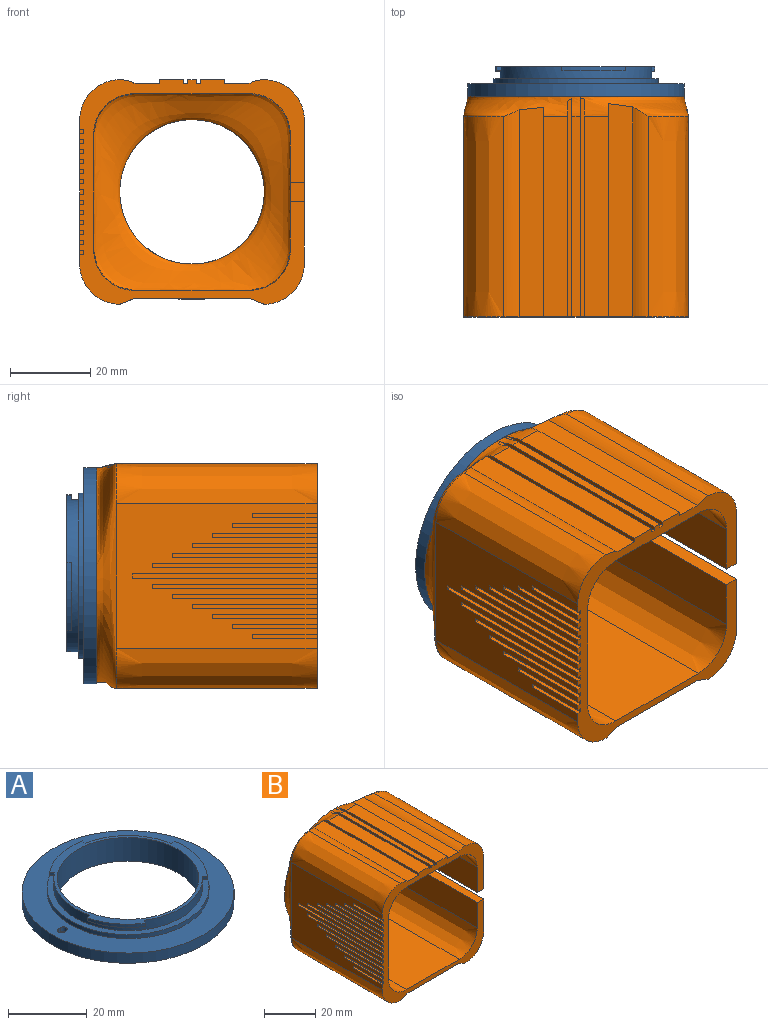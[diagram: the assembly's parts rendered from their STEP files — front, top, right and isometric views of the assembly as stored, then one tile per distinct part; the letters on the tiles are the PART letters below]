
ASSEMBLY  parts=2 mates=1
PART A: 25 faces, bbox 54x54x7.4 mm
  f0: cylinder r=18.92mm len=37.85mm, axis (0,0,-1), area 300.8mm2, adj f6,f7,f8,f10,f11,f13,f14,f15
  f1: cylinder r=18.03mm len=36.07mm, axis (0,0,-1), area 836.1mm2, adj f4,f7
  f2: cylinder r=27mm len=54mm, axis (0,0,-1), area 538.6mm2, adj f3,f4
  f3: plane 54x54mm, normal (0,0,1), area 948.2mm2, adj f2,f5,f20,f21,f22,f23
  f4: plane 54x54mm, normal (0,0,-1), area 1268.5mm2, adj f1,f2
  f5: cylinder r=20.63mm len=41.26mm, axis (0,0,-1), area 164.6mm2, adj f3,f6
  f6: plane 41.26x41.26mm, normal (0,0,1), area 212.3mm2, adj f0,f5
  f7: plane 39.82x39.14mm, normal (0,0,1), area 166.2mm2, adj f0,f1,f8,f9,f10,f12,f13,f14
  f8: plane 1.27x1.02mm, normal (0.98,-0.17,0), area 1.3mm2, adj f0,f7,f9,f11
  f9: cylinder r=20.21mm len=15.81mm, axis (0,0,1), area 17mm2, adj f7,f8,f10,f11
  f10: plane 1.02x1.02mm, normal (-0.79,-0.61,0), area 1.3mm2, adj f0,f7,f9,f11
  f11: plane 15.81x5.2mm, normal (0,0,-1), area 20.9mm2, adj f0,f8,f9,f10
  f12: cylinder r=20.21mm len=12.16mm, axis (0,0,1), area 15.6mm2, adj f7,f13,f14,f15
  f13: plane 1.09x1.02mm, normal (0.84,-0.54,0), area 1.3mm2, adj f0,f7,f12,f15
  f14: plane 1.25x1.02mm, normal (-0.24,0.97,0), area 1.3mm2, adj f0,f7,f12,f15
  f15: plane 12.47x9.44mm, normal (0,0,-1), area 19.2mm2, adj f0,f12,f13,f14
  f16: plane 1.27x1.02mm, normal (-0.17,0.99,0), area 1.3mm2, adj f0,f7,f18,f19
  f17: plane 1.02x0.95mm, normal (-0.68,-0.74,0), area 1.3mm2, adj f0,f7,f18,f19
  f18: cylinder r=20.21mm len=16.99mm, axis (0,0,1), area 18.6mm2, adj f7,f16,f17,f19
  f19: plane 16.99x6.26mm, normal (0,0,-1), area 22.9mm2, adj f0,f16,f17,f18
  f20: cylinder r=1.02mm len=2.03mm, axis (0,0,1), area 4.1mm2, adj f3,f21,f23,f24
  f21: plane 1.27x0.76mm, normal (0,-1,0), area 1mm2, adj f3,f20,f22,f24
  f22: cylinder r=1.02mm len=2.03mm, axis (0,0,1), area 4.1mm2, adj f3,f21,f23,f24
  f23: plane 1.27x0.76mm, normal (0,1,0), area 1mm2, adj f3,f20,f22,f24
  f24: plane 2.79x2.03mm, normal (0,0,1), area 4.8mm2, adj f20,f21,f22,f23
PART B: 120 faces, bbox 56.8x55.8x56.8 mm
  f0: plane 50x15.6mm, normal (1,0,0), area 460mm2, adj f2,f6,f10,f11,f99,f100,f101,f102
  f1: plane 54.46x53.95mm, normal (0,1,0), area 1265.1mm2, adj f2,f9,f92
  f2: bspline ~56x56mm, area 1121.8mm2, adj f0,f1,f3,f4,f5,f7,f8,f11
  f3: plane 50.07x6.07mm, normal (0,0,1), area 300mm2, adj f2,f6,f84,f89
  f4: plane 50x2mm, normal (0,0,1), area 100mm2, adj f2,f6,f78,f86
  f5: plane 50.07x6.07mm, normal (0,0,1), area 300mm2, adj f2,f6,f80,f81
  f6: plane 56x56mm, normal (0,-1,0), area 640mm2, adj f0,f3,f4,f5,f7,f10,f11,f12
  f7: plane 50x36mm, normal (-1,0,0), area 1412mm2, adj f2,f6,f12,f13,f26,f27,f28,f30
  f8: plane 4.8x3.5mm, normal (0,-1,0), area 16.8mm2, adj f2,f9,f10,f16
  f9: bspline ~49x49mm, area 1542.6mm2, adj f1,f8,f17,f18,f19,f20,f21,f22
  f10: plane 50x3.5mm, normal (0,0,-1), area 175mm2, adj f0,f6,f8,f25
  f11: extruded ~50x10mm, area 785.4mm2, adj f0,f2,f6,f83
  f12: extruded ~50x10mm, area 785.4mm2, adj f2,f6,f7,f87
  f13: extruded ~50x10mm, area 785.4mm2, adj f2,f6,f7,f90
  f14: extruded ~50x10mm, area 785.4mm2, adj f2,f6,f15,f91
  f15: plane 50x15.6mm, normal (1,0,0), area 544.4mm2, adj f2,f6,f14,f16,f93,f95,f97
  f16: plane 50x3.5mm, normal (0,0,1), area 175mm2, adj f6,f8,f15,f17
  f17: plane 50.66x12.76mm, normal (-1,0,0), area 605mm2, adj f6,f9,f16,f18
  f18: extruded ~50x10mm, area 785.4mm2, adj f6,f9,f17,f19
  f19: plane 50.81x29.81mm, normal (0,0,1), area 1450mm2, adj f6,f9,f18,f20
  f20: extruded ~50x10mm, area 785.4mm2, adj f6,f9,f19,f21
  f21: plane 50.81x29.81mm, normal (1,0,0), area 1450mm2, adj f6,f9,f20,f22
  f22: extruded ~50x10mm, area 785.4mm2, adj f6,f9,f21,f23
  f23: plane 50.81x29.81mm, normal (0,0,-1), area 1450mm2, adj f6,f9,f22,f24
  f24: extruded ~50x10mm, area 785.4mm2, adj f6,f9,f23,f25
  f25: plane 50.66x12.76mm, normal (-1,0,0), area 605mm2, adj f6,f9,f10,f24
  f26: plane 46x1mm, normal (0,0,-1), area 46mm2, adj f6,f7,f27,f29
  f27: plane 1x1mm, normal (0,-1,0), area 1mm2, adj f7,f26,f28,f29
  f28: plane 46x1mm, normal (0,0,1), area 46mm2, adj f6,f7,f27,f29
  f29: plane 46x1mm, normal (-1,0,0), area 46mm2, adj f6,f26,f27,f28
  f30: plane 1x1mm, normal (0,-1,0), area 1mm2, adj f7,f31,f32,f33
  f31: plane 21x1mm, normal (0,0,1), area 21mm2, adj f6,f7,f30,f33
  f32: plane 21x1mm, normal (0,0,-1), area 21mm2, adj f6,f7,f30,f33
  f33: plane 21x1mm, normal (-1,0,0), area 21mm2, adj f6,f30,f31,f32
  f34: plane 1x1mm, normal (0,-1,0), area 1mm2, adj f7,f35,f36,f37
  f35: plane 31x1mm, normal (0,0,1), area 31mm2, adj f6,f7,f34,f37
  f36: plane 31x1mm, normal (0,0,-1), area 31mm2, adj f6,f7,f34,f37
  f37: plane 31x1mm, normal (-1,0,0), area 31mm2, adj f6,f34,f35,f36
  f38: plane 16x1mm, normal (0,0,1), area 16mm2, adj f6,f7,f40,f41
  f39: plane 16x1mm, normal (0,0,-1), area 16mm2, adj f6,f7,f40,f41
  f40: plane 1x1mm, normal (0,-1,0), area 1mm2, adj f7,f38,f39,f41
  f41: plane 16x1mm, normal (-1,0,0), area 16mm2, adj f6,f38,f39,f40
  f42: plane 16x1mm, normal (0,0,-1), area 16mm2, adj f6,f7,f43,f45
  f43: plane 1x1mm, normal (0,-1,0), area 1mm2, adj f7,f42,f44,f45
  f44: plane 16x1mm, normal (0,0,1), area 16mm2, adj f6,f7,f43,f45
  f45: plane 16x1mm, normal (-1,0,0), area 16mm2, adj f6,f42,f43,f44
  f46: plane 41x1mm, normal (0,0,1), area 41mm2, adj f6,f7,f48,f49
  f47: plane 41x1mm, normal (0,0,-1), area 41mm2, adj f6,f7,f48,f49
  f48: plane 1x1mm, normal (0,-1,0), area 1mm2, adj f7,f46,f47,f49
  f49: plane 41x1mm, normal (-1,0,0), area 41mm2, adj f6,f46,f47,f48
  f50: plane 36x1mm, normal (0,0,1), area 36mm2, adj f6,f7,f52,f53
  f51: plane 36x1mm, normal (0,0,-1), area 36mm2, adj f6,f7,f52,f53
  f52: plane 1x1mm, normal (0,-1,0), area 1mm2, adj f7,f50,f51,f53
  f53: plane 36x1mm, normal (-1,0,0), area 36mm2, adj f6,f50,f51,f52
  f54: plane 31x1mm, normal (0,0,1), area 31mm2, adj f6,f7,f56,f57
  f55: plane 31x1mm, normal (0,0,-1), area 31mm2, adj f6,f7,f56,f57
  f56: plane 1x1mm, normal (0,-1,0), area 1mm2, adj f7,f54,f55,f57
  f57: plane 31x1mm, normal (-1,0,0), area 31mm2, adj f6,f54,f55,f56
  f58: plane 26x1mm, normal (0,0,1), area 26mm2, adj f6,f7,f60,f61
  f59: plane 26x1mm, normal (0,0,-1), area 26mm2, adj f6,f7,f60,f61
  f60: plane 1x1mm, normal (0,-1,0), area 1mm2, adj f7,f58,f59,f61
  f61: plane 26x1mm, normal (-1,0,0), area 26mm2, adj f6,f58,f59,f60
  f62: plane 1x1mm, normal (0,-1,0), area 1mm2, adj f7,f63,f64,f65
  f63: plane 36x1mm, normal (0,0,1), area 36mm2, adj f6,f7,f62,f65
  f64: plane 36x1mm, normal (0,0,-1), area 36mm2, adj f6,f7,f62,f65
  f65: plane 36x1mm, normal (-1,0,0), area 36mm2, adj f6,f62,f63,f64
  f66: plane 41x1mm, normal (0,0,-1), area 41mm2, adj f6,f7,f67,f69
  f67: plane 1x1mm, normal (0,-1,0), area 1mm2, adj f7,f66,f68,f69
  f68: plane 41x1mm, normal (0,0,1), area 41mm2, adj f6,f7,f67,f69
  f69: plane 41x1mm, normal (-1,0,0), area 41mm2, adj f6,f66,f67,f68
  f70: plane 1x1mm, normal (0,-1,0), area 1mm2, adj f7,f71,f72,f73
  f71: plane 26x1mm, normal (0,0,1), area 26mm2, adj f6,f7,f70,f73
  f72: plane 26x1mm, normal (0,0,-1), area 26mm2, adj f6,f7,f70,f73
  f73: plane 26x1mm, normal (-1,0,0), area 26mm2, adj f6,f70,f71,f72
  f74: plane 21x1mm, normal (0,0,1), area 21mm2, adj f6,f7,f76,f77
  f75: plane 21x1mm, normal (0,0,-1), area 21mm2, adj f6,f7,f76,f77
  f76: plane 1x1mm, normal (0,-1,0), area 1mm2, adj f7,f74,f75,f77
  f77: plane 21x1mm, normal (-1,0,0), area 21mm2, adj f6,f74,f75,f76
  f78: plane 54.62x1mm, normal (1,0,0), area 52.4mm2, adj f2,f4,f6,f79
  f79: plane 54.67x1.05mm, normal (0,0,1), area 54.5mm2, adj f2,f6,f78,f80
  f80: plane 54.32x1mm, normal (-1,0,0), area 52.4mm2, adj f2,f5,f6,f79
  f81: plane 53.19x1mm, normal (1,0,0), area 52.2mm2, adj f2,f5,f6,f82
  f82: plane 53.31x6.25mm, normal (0,0,1), area 323.4mm2, adj f2,f6,f81,f83
  f83: cylinder r=8mm len=52.36mm, axis (0,-1,0), area 206.9mm2, adj f2,f6,f11,f82
  f84: plane 53.79x1mm, normal (1,0,0), area 52mm2, adj f2,f3,f6,f85
  f85: plane 54.54x1.06mm, normal (0,0,1), area 54.1mm2, adj f2,f6,f84,f86
  f86: plane 54.47x1mm, normal (-1,0,0), area 52.1mm2, adj f2,f4,f6,f85
  f87: cylinder r=8mm len=51.65mm, axis (0,-1,0), area 205.5mm2, adj f2,f6,f12,f88
  f88: plane 52.41x6.29mm, normal (0,0,1), area 318.1mm2, adj f2,f6,f87,f89
  f89: plane 52.45x1.21mm, normal (-1,0,0), area 51.4mm2, adj f2,f3,f6,f88
  f90: plane 52.62x3.71mm, normal (0.37,0,-0.93), area 207.1mm2, adj f2,f6,f13,f92
  f91: plane 52.04x3.71mm, normal (-0.37,0,-0.93), area 205mm2, adj f2,f6,f14,f92
  f92: plane 55x28.58mm, normal (0,0,-1), area 1538mm2, adj f1,f2,f6,f90,f91
  f93: cylinder r=5mm len=10mm, axis (1,0,0), area 31.4mm2, adj f15,f94
  f94: plane 10x10mm, normal (1,0,0), area 78.5mm2, adj f93
  f95: cylinder r=5mm len=10mm, axis (1,0,0), area 31.4mm2, adj f15,f96
  f96: plane 10x10mm, normal (1,0,0), area 78.5mm2, adj f95
  f97: cylinder r=5mm len=10mm, axis (1,0,0), area 31.4mm2, adj f15,f98
  f98: plane 10x10mm, normal (1,0,0), area 78.5mm2, adj f97
  f99: plane 5x4mm, normal (0,0.78,0.62), area 6.4mm2, adj f0,f100,f104,f105
  f100: plane 4x1mm, normal (0,0,1), area 4mm2, adj f0,f99,f101,f105
  f101: plane 5x4mm, normal (0,-0.78,-0.62), area 6.4mm2, adj f0,f100,f102,f105
  f102: plane 5x4mm, normal (0,-0.78,0.62), area 6.4mm2, adj f0,f101,f103,f105
  f103: plane 4x1mm, normal (0,0,-1), area 4mm2, adj f0,f102,f104,f105
  f104: plane 5x4mm, normal (0,0.78,-0.62), area 6.4mm2, adj f0,f99,f103,f105
  f105: plane 10x8mm, normal (1,0,0), area 40mm2, adj f99,f100,f101,f102,f103,f104
  f106: plane 3x1mm, normal (0,0,-1), area 3mm2, adj f0,f107,f111,f112
  f107: plane 5x4mm, normal (0,0.78,-0.62), area 6.4mm2, adj f0,f106,f108,f112
  f108: plane 5x4mm, normal (0,0.78,0.62), area 6.4mm2, adj f0,f107,f109,f112
  f109: plane 3x1mm, normal (0,0,1), area 3mm2, adj f0,f108,f110,f112
  f110: plane 5x4mm, normal (0,-0.78,-0.62), area 6.4mm2, adj f0,f109,f111,f112
  f111: plane 5x4mm, normal (0,-0.78,0.62), area 6.4mm2, adj f0,f106,f110,f112
  f112: plane 10x7mm, normal (1,0,0), area 30mm2, adj f106,f107,f108,f109,f110,f111
  f113: plane 5x4mm, normal (0,-0.78,0.62), area 6.4mm2, adj f0,f114,f118,f119
  f114: plane 25x1mm, normal (0,0,-1), area 25mm2, adj f0,f113,f115,f119
  f115: plane 5x4mm, normal (0,0.78,-0.62), area 6.4mm2, adj f0,f114,f116,f119
  f116: plane 5x4mm, normal (0,0.78,0.62), area 6.4mm2, adj f0,f115,f117,f119
  f117: plane 25x1mm, normal (0,0,1), area 25mm2, adj f0,f116,f118,f119
  f118: plane 5x4mm, normal (0,-0.78,-0.62), area 6.4mm2, adj f0,f113,f117,f119
  f119: plane 29x10mm, normal (1,0,0), area 250mm2, adj f113,f114,f115,f116,f117,f118
PLACE A rot(axis=(0,0.71,0.71),180deg) t=(0.12,-3.18,0)mm
PLACE B t=(0.12,-3.18,-0.07)mm
MATE fastened B.f1 <-> A.f0  axis (0,1,0) through (0.12,-3.18,0)mm
